# Revit family: 57_CRD_ME_Climarad_2-0
name_source: partatom
category: Mechanical Equipment
units: mm (PartAtom-declared; Revit-internal decimal feet)

## family parameters
Always vertical = Yes
Classification = None
Cut with Voids When Loaded = Yes
Part Type = Normal
Room Calculation Point = Yes
Round Connector Dimension = Use Diameter
Shared = No
Work Plane-Based = Yes

## types (14) — shared parameters
Default Elevation = 1219 mm
Description = ClimaRad Sensa H2X ventilatie-unit
Manufacturer = ClimaRad
Model = Sensa H2X
diameter_cv = 15 mm  [stored 0.0492126 ft]
diepte_achterunit = 135 mm  [stored 0.442913 ft]
diepte_kast = 197 mm
hart_doorvoer_tov_ok_kast = 367 mm  [stored 1.20407 ft]
hart_ventilatie_doorvoer_tov_onderkant_unit = 385 mm  [stored 1.26312 ft]
hoh_ventilatie_doorvoeren = 1098 mm  [stored 3.60236 ft]
hoogte_unit = 466 mm  [stored 1.52887 ft]
invoer_cv = 0.0 L/s
lengte_onderstel = 700 mm  [stored 2.29659 ft]
lengte_unit = 1240 mm  [stored 4.06824 ft]
positie_wcd_uit_hart_unit = 750 mm  [stored 2.46063 ft]
schacht = Yes
voltage = 230 V

## per-type parameters (varying)
| type | cv_aanvoer | diepte | hoogte_kast | lengte_kast | type_kap |
| 21s-400 - lengte 2800mm | 1310 mm  [stored 4.2979 ft] | 211 mm  [stored 0.692257 ft] | 404 mm  [stored 1.32546 ft] | 2800 mm  [stored 9.18635 ft] | 57_CRD_ME_kap_climarad_2-0 : diepte 70 mm |
| 21s-400 - lengte 2400mm | 1110 mm  [stored 3.64173 ft] | 211 mm  [stored 0.692257 ft] | 404 mm  [stored 1.32546 ft] | 2400 mm | 57_CRD_ME_kap_climarad_2-0 : diepte 70 mm |
| 21s-400 - lengte 2200mm | 1010 mm  [stored 3.31365 ft] | 211 mm  [stored 0.692257 ft] | 404 mm  [stored 1.32546 ft] | 2200 mm | 57_CRD_ME_kap_climarad_2-0 : diepte 70 mm |
| 21s-400 - lengte 1800mm | 810 mm | 211 mm  [stored 0.692257 ft] | 404 mm  [stored 1.32546 ft] | 1800 mm  [stored 5.90551 ft] | 57_CRD_ME_kap_climarad_2-0 : diepte 70 mm |
| 21s-400 - lengte 1500mm | 660 mm | 211 mm  [stored 0.692257 ft] | 404 mm  [stored 1.32546 ft] | 1800 mm  [stored 5.90551 ft] | 57_CRD_ME_kap_climarad_2-0 : diepte 70 mm |
| 21s-500 - lengte 2800mm | 1310 mm  [stored 4.2979 ft] | 211 mm  [stored 0.692257 ft] | 504 mm  [stored 1.65354 ft] | 2800 mm  [stored 9.18635 ft] | 57_CRD_ME_kap_climarad_2-0 : diepte 70 mm |
| 21s-500 - lengte 2400mm | 1110 mm  [stored 3.64173 ft] | 211 mm  [stored 0.692257 ft] | 504 mm  [stored 1.65354 ft] | 2400 mm | 57_CRD_ME_kap_climarad_2-0 : diepte 70 mm |
| 21s-500 - lengte 2200mm | 1010 mm  [stored 3.31365 ft] | 211 mm  [stored 0.692257 ft] | 504 mm  [stored 1.65354 ft] | 2200 mm | 57_CRD_ME_kap_climarad_2-0 : diepte 70 mm |
| 21s-500 - lengte 1800mm | 810 mm | 211 mm  [stored 0.692257 ft] | 504 mm  [stored 1.65354 ft] | 1800 mm  [stored 5.90551 ft] | 57_CRD_ME_kap_climarad_2-0 : diepte 70 mm |
| 21s-500 - lengte 1500mm | 660 mm | 211 mm  [stored 0.692257 ft] | 504 mm  [stored 1.65354 ft] | 1500 mm  [stored 4.92126 ft] | 57_CRD_ME_kap_climarad_2-0 : diepte 70 mm |
| 22s-400 - lengte 2400mm | 1110 mm  [stored 3.64173 ft] | 243 mm | 404 mm  [stored 1.32546 ft] | 2400 mm | 57_CRD_ME_kap_climarad_2-0 : diepte 102 mm |
| 22s-400 - lengte 2200mm | 1010 mm  [stored 3.31365 ft] | 243 mm | 404 mm  [stored 1.32546 ft] | 2200 mm | 57_CRD_ME_kap_climarad_2-0 : diepte 102 mm |
| 22s-500 - lengte 2400mm | 1110 mm  [stored 3.64173 ft] | 243 mm | 504 mm  [stored 1.65354 ft] | 2400 mm | 57_CRD_ME_kap_climarad_2-0 : diepte 102 mm |
| 22s-500 - lengte 2200mm | 1010 mm  [stored 3.31365 ft] | 243 mm | 504 mm  [stored 1.65354 ft] | 2200 mm | 57_CRD_ME_kap_climarad_2-0 : diepte 102 mm |

note: [stored X ft] marks values corroborated as IEEE doubles in the binary element streams (Revit-internal decimal feet)

## geometry (parser evidence)
native form markers: Sweep x13
no freeform markers — native parametric forms only
